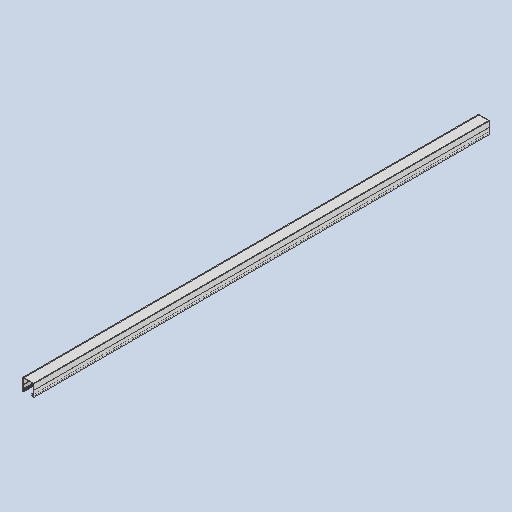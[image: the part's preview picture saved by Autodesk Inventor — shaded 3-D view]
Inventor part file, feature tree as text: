
AUTODESK INVENTOR PART (.ipt)
format: ipt  version: 2022 (Build 260153000, 153)  size: 101,376 bytes
history: native  units: in
note: dims shown in document units (in); Inventor stores cm internally (conversion verified against a paired STEP export)
features: extrude x1
ambient origin geometry x8: Origin, YZ Plane, XZ Plane, XY Plane, X Axis, Y Axis, Z Axis, Center Point
bodies: Solid1 (feature_tree)
feature tree (1):
  extrude  "Extrusion1"  [1 undecoded]
note: 1 required parameter value undecoded (feature->parameter linkage not recoverable at this tier; creation-order binding heuristic only, values carry confidence <= 0.55)
